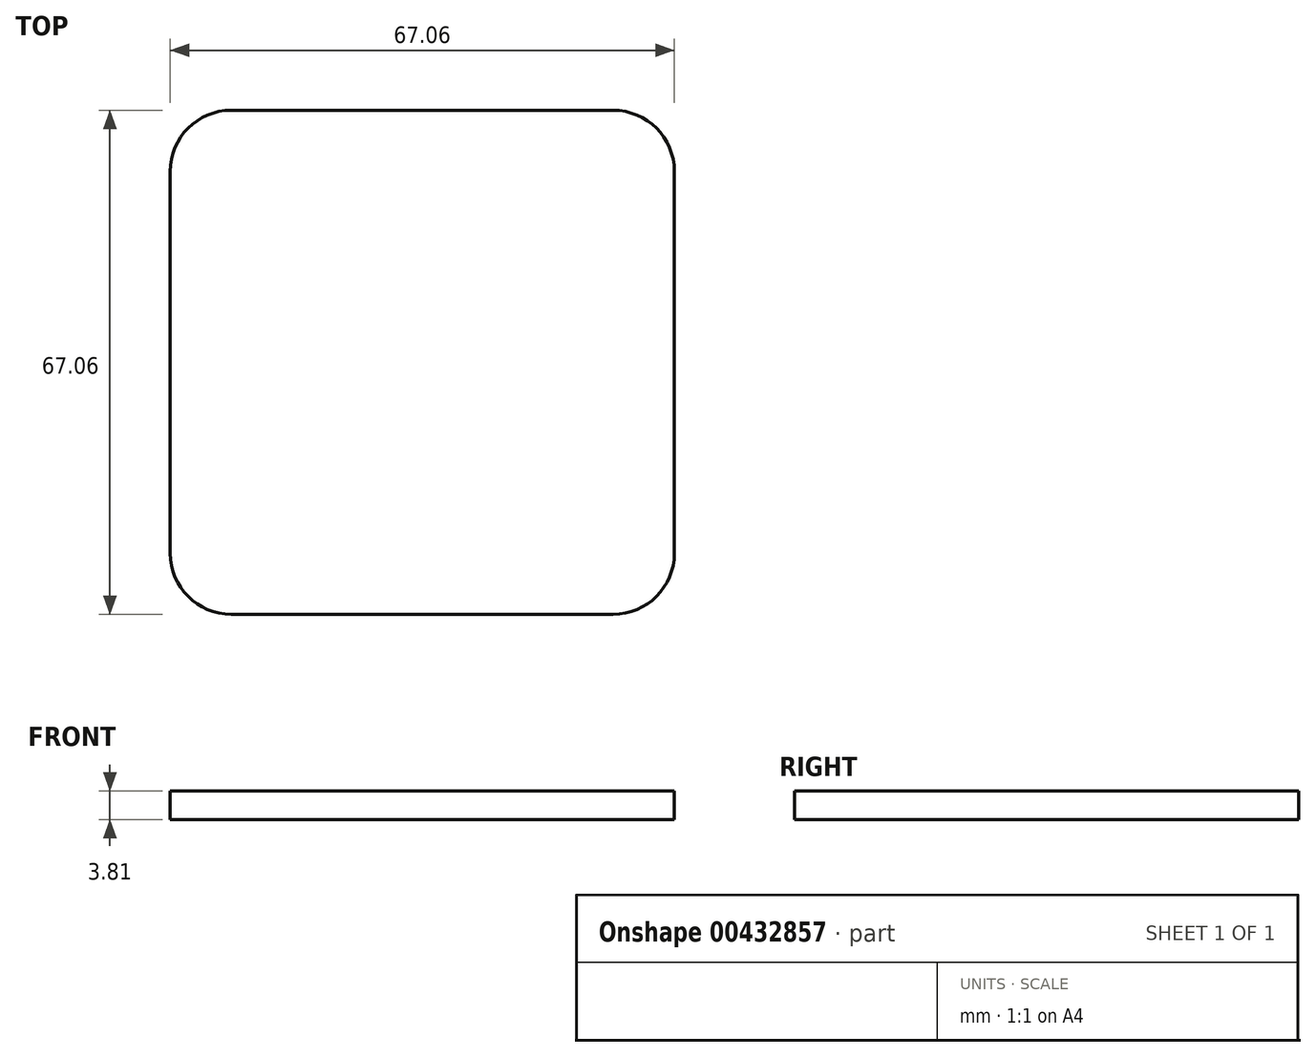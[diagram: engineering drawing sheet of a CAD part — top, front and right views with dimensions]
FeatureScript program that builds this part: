
annotation { "Feature Type Name" : "Feature", "Feature Type Description" : "" }
export const myFeature = defineFeature(function(context is Context, id is Id, definition is map)
    precondition{}
    {
        {
            var Q0;
            Q0=qCreatedBy(makeId("Top.planeOp"),FACE);
            var sketch = newSketch(context, id + "F0", { "sketchPlane" : qUnion([Q0])});
            skLineSegment(sketch, "E0.bottom", {"start": v(-25.4, 38.1) * mm, "end": v(25.4, 38.1) * mm});
            skLineSegment(sketch, "E0.top", {"start": v(-25.4, -38.1) * mm, "end": v(25.4, -38.1) * mm});
            skLineSegment(sketch, "E0.left", {"start": v(-38.1, 25.4) * mm, "end": v(-38.1, -25.4) * mm});
            skLineSegment(sketch, "E0.right", {"start": v(38.1, 25.4) * mm, "end": v(38.1, -25.4) * mm});
            skPoint(sketch, "E1.visualSharp", {"position": v(-38.1, 38.1) * mm});
            skArc(sketch, "E1.filletArc", {"start": v(-25.4, 38.1) * mm, "mid": v(-34.38, 34.38) * mm, "end": v(-38.1, 25.4) * mm});
            skPoint(sketch, "E2.visualSharp", {"position": v(38.1, 38.1) * mm});
            skArc(sketch, "E2.filletArc", {"start": v(38.1, 25.4) * mm, "mid": v(34.38, 34.38) * mm, "end": v(25.4, 38.1) * mm});
            skPoint(sketch, "E3.visualSharp", {"position": v(-38.1, -38.1) * mm});
            skArc(sketch, "E3.filletArc", {"start": v(-38.1, -25.4) * mm, "mid": v(-34.38, -34.38) * mm, "end": v(-25.4, -38.1) * mm});
            skPoint(sketch, "E4.visualSharp", {"position": v(38.1, -38.1) * mm});
            skArc(sketch, "E4.filletArc", {"start": v(25.4, -38.1) * mm, "mid": v(34.38, -34.38) * mm, "end": v(38.1, -25.4) * mm});
            skLineSegment(sketch, "E5", {"start": v(-25.4, 25.4) * mm, "end": v(25.4, -25.4) * mm, "construction": true});
            skLineSegment(sketch, "E6", {"start": v(25.4, 25.4) * mm, "end": v(-25.4, -25.4) * mm, "construction": true});
            skLineSegment(sketch, "E7", {"start": v(0, -42.48) * mm, "end": v(0, 0) * mm, "construction": true});
            skArc(sketch, "E8.0", {"start": v(-25.4, 33.53) * mm, "mid": v(-31.15, 31.15) * mm, "end": v(-33.53, 25.4) * mm});
            skLineSegment(sketch, "E8.1", {"start": v(-33.53, 25.4) * mm, "end": v(-33.53, -25.4) * mm});
            skLineSegment(sketch, "E8.2", {"start": v(-25.4, 33.53) * mm, "end": v(25.4, 33.53) * mm});
            skArc(sketch, "E8.3", {"start": v(-33.53, -25.4) * mm, "mid": v(-31.15, -31.15) * mm, "end": v(-25.4, -33.53) * mm});
            skArc(sketch, "E8.4", {"start": v(33.53, 25.4) * mm, "mid": v(31.15, 31.15) * mm, "end": v(25.4, 33.53) * mm});
            skLineSegment(sketch, "E8.5", {"start": v(33.53, 25.4) * mm, "end": v(33.53, -25.4) * mm});
            skArc(sketch, "E8.6", {"start": v(25.4, -33.53) * mm, "mid": v(31.15, -31.15) * mm, "end": v(33.53, -25.4) * mm});
            skLineSegment(sketch, "E8.7", {"start": v(-25.4, -33.53) * mm, "end": v(25.4, -33.53) * mm});
            skSolve(sketch);
        }
        {
            var Q0;
            Q0=makeQuery(id+"F0.imprint","IMPRINT",FACE,{"disambiguationData":[TD([[makeQuery(id+"F0.imprint","IMPRINT",EDGE,{"derivedFrom":sQuery(id+"F0.wireOp",EDGE,"E8.0")}),1.0]])]});
            extrude(context, id + "F1", {"entities" : qUnion([Q0]), "depth" : 3.8 * mm});
        }
    });
